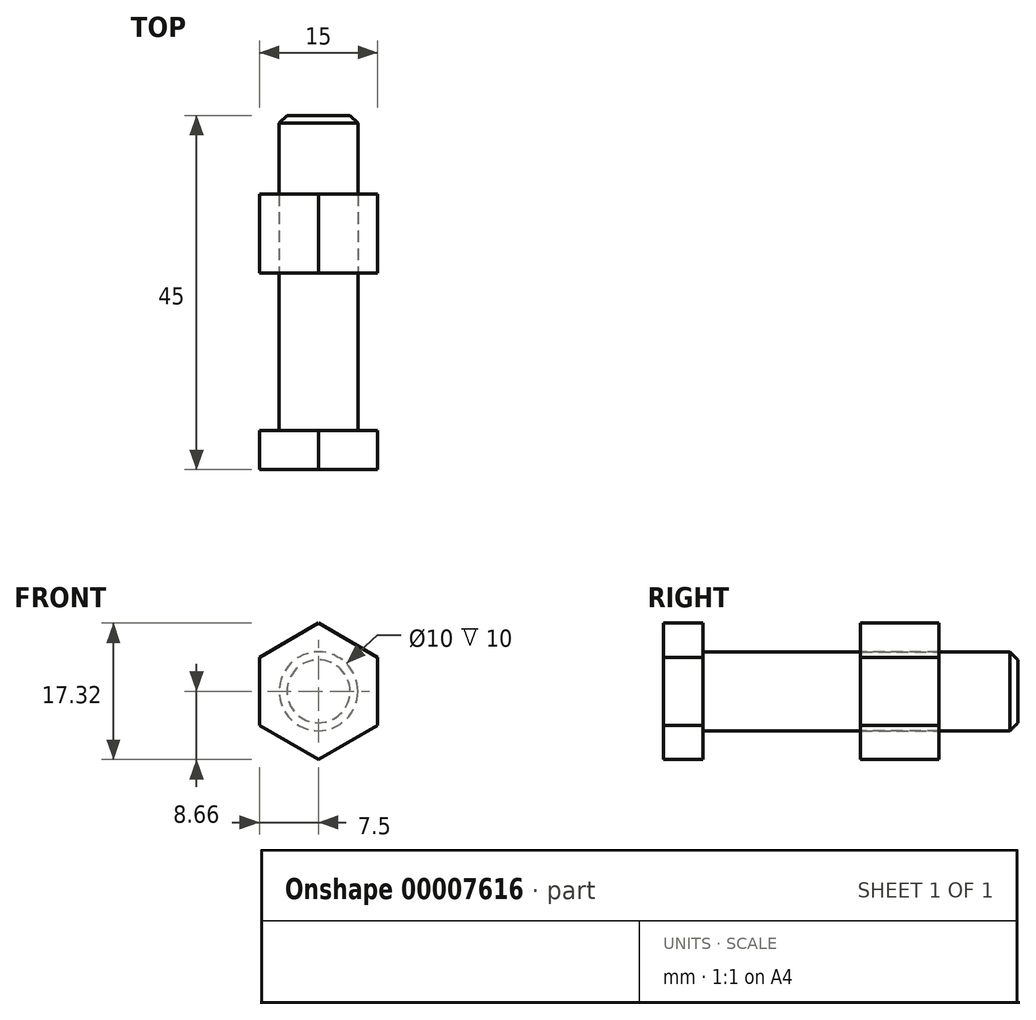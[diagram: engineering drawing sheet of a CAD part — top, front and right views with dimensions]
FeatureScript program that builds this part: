
annotation { "Feature Type Name" : "Feature", "Feature Type Description" : "" }
export const myFeature = defineFeature(function(context is Context, id is Id, definition is map)
    precondition{}
    {
        {
            var Q0;
            Q0=qCreatedBy(makeId("Front.planeOp"),FACE);
            var sketch = newSketch(context, id + "F0", { "sketchPlane" : qUnion([Q0])});
            skCircle(sketch, "E0", {"center": v(0, 0) * mm, "radius": 5 * mm});
            skSolve(sketch);
        }
        {
            var Q0;
            Q0 = qSketchRegion(id + "F0", true);
            extrude(context, id + "F1", {"entities" : qUnion([Q0]), "depth" : 40 * mm});
        }
        {
            var Q0;
            Q0=makeQuery(id+"F1.opExtrude","CAP_FACE",FACE,{"disambiguationData":[OSD([sQuery(id+"F0.wireOp",EDGE,"E0")])],"isStart":false});
            var sketch = newSketch(context, id + "F2", { "sketchPlane" : qUnion([Q0])});
            skCircle(sketch, "E1.cCircle", {"center": v(0, 0) * mm, "radius": 7.5 * mm, "construction": true});
            skLineSegment(sketch, "E1.0", {"start": v(-7.5, -4.33) * mm, "end": v(-7.5, 4.33) * mm});
            skLineSegment(sketch, "E1.1", {"start": v(-7.5, 4.33) * mm, "end": v(0, 8.66) * mm});
            skLineSegment(sketch, "E1.2", {"start": v(0, 8.66) * mm, "end": v(7.5, 4.33) * mm});
            skLineSegment(sketch, "E1.3", {"start": v(7.5, 4.33) * mm, "end": v(7.5, -4.33) * mm});
            skLineSegment(sketch, "E1.4", {"start": v(7.5, -4.33) * mm, "end": v(0, -8.66) * mm});
            skLineSegment(sketch, "E1.5", {"start": v(0, -8.66) * mm, "end": v(-7.5, -4.33) * mm});
            skPoint(sketch, "E1.0.midPoint", {"position": v(-7.5, 0) * mm});
            skSolve(sketch);
        }
        {
            var Q0;
            Q0 = qSketchRegion(id + "F2", true);
            extrude(context, id + "F3", {"entities" : qUnion([Q0]), "operationType" : NewBodyOperationType.ADD, "depth" : 5 * mm});
        }
        {
            var Q0;
            Q0=makeQuery(id+"F1.opExtrude","CAP_EDGE",EDGE,{"disambiguationData":[OSD([sQuery(id+"F0.wireOp",EDGE,"E0")])],"isStart":true});
            chamfer(context, id + "F4", {"entities" : qUnion([Q0]), "width" : 1 * mm, "tangentPropagation" : true});
        }
        {
            var Q0;
            Q0=makeQuery(id+"F3.opExtrude","CAP_FACE",FACE,{"disambiguationData":[OSD([sQuery(id+"F2.wireOp",EDGE,"E1.0"),sQuery(id+"F2.wireOp",EDGE,"E1.1"),sQuery(id+"F2.wireOp",EDGE,"E1.2"),sQuery(id+"F2.wireOp",EDGE,"E1.3"),sQuery(id+"F2.wireOp",EDGE,"E1.4"),sQuery(id+"F2.wireOp",EDGE,"E1.5")])],"isStart":true});
            cPlane(context, id + "F5", {"entities" : qUnion([Q0]), "cplaneType" : CPlaneType.OFFSET, "offset" : 20 * mm, "width" : 150 * mm, "height" : 150 * mm});
        }
        {
            var Q0;
            Q0=qCreatedBy(id+"F5.planeOp",FACE);
            var sketch = newSketch(context, id + "F6", { "sketchPlane" : qUnion([Q0])});
            skCircle(sketch, "E2", {"center": v(0, 0) * mm, "radius": 5 * mm});
            skCircle(sketch, "E3.cCircle", {"center": v(0, 0) * mm, "radius": 7.5 * mm, "construction": true});
            skLineSegment(sketch, "E3.0", {"start": v(-7.5, -4.33) * mm, "end": v(-7.5, 4.33) * mm});
            skLineSegment(sketch, "E3.1", {"start": v(-7.5, 4.33) * mm, "end": v(0, 8.66) * mm});
            skLineSegment(sketch, "E3.2", {"start": v(0, 8.66) * mm, "end": v(7.5, 4.33) * mm});
            skLineSegment(sketch, "E3.3", {"start": v(7.5, 4.33) * mm, "end": v(7.5, -4.33) * mm});
            skLineSegment(sketch, "E3.4", {"start": v(7.5, -4.33) * mm, "end": v(0, -8.66) * mm});
            skLineSegment(sketch, "E3.5", {"start": v(0, -8.66) * mm, "end": v(-7.5, -4.33) * mm});
            skPoint(sketch, "E3.0.midPoint", {"position": v(-7.5, 0) * mm});
            skSolve(sketch);
        }
        {
            var Q0;
            Q0 = qSketchRegion(id + "F6", true);
            extrude(context, id + "F7", {"entities" : qUnion([Q0]), "depth" : 10 * mm});
        }
    });
